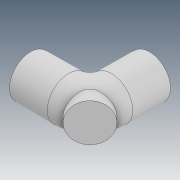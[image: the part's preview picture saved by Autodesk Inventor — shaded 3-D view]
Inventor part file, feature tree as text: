
AUTODESK INVENTOR PART (.ipt)
format: ipt  version: 2020 (Build 240168000, 168)  size: 182,272 bytes
history: native  units: mm
features: sketch x4, revolve x3, plane x2, extrude x1, projected_geometry x1
ambient origin geometry x8: Origin, YZ Plane, XZ Plane, XY Plane, X Axis, Y Axis, Z Axis, Center Point
bodies: Solid1 (feature_tree)
feature tree (11):
  revolve  "Revolution1"  [1 undecoded]
  revolve  "Revolution2"  [1 undecoded]
  revolve  "Revolution3"  [1 undecoded]
  plane  "Work Plane2"
  extrude  "Extrusion1"  Depth=10.0mm
  sketch  "Sketch1"  dims[d0=11.0mm d1=20.0mm]
  sketch  "Sketch2"  dims[d2=11.2mm d3=1.6mm]
  sketch  "Sketch3"  dims[d4=90.0deg d5=11.2mm]
  plane  "Work Plane1"
  sketch  "Sketch4"  dims[d6=90.0deg d7=20.0mm d8=90.0deg d9=11.0mm d10=1.6mm d11=90.0deg d12=-7.853982mm d13=30.0mm d14=20.0mm d15=10.0mm d16=0.0mm]
  projected_geometry  "Projected Loop1"
note: 3 required parameter values undecoded (feature->parameter linkage not recoverable at this tier; creation-order binding heuristic only, values carry confidence <= 0.55)
